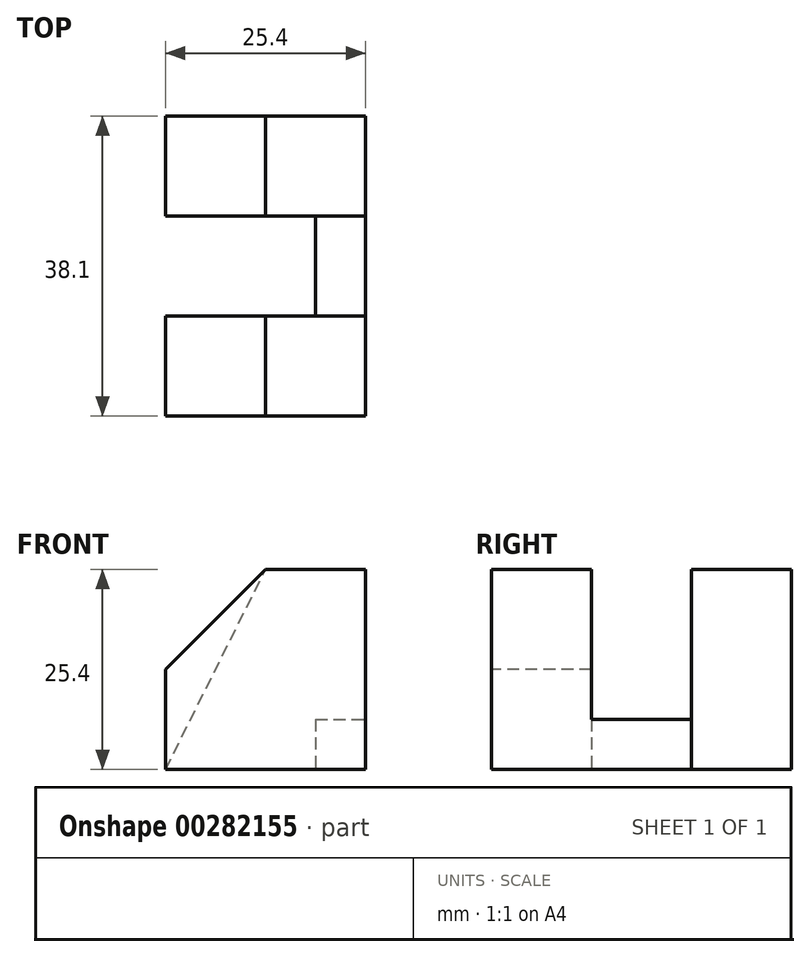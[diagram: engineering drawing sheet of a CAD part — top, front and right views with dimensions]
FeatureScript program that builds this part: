
annotation { "Feature Type Name" : "Feature", "Feature Type Description" : "" }
export const myFeature = defineFeature(function(context is Context, id is Id, definition is map)
    precondition{}
    {
        {
            var Q0;
            Q0=qCreatedBy(makeId("Front.planeOp"),FACE);
            var sketch = newSketch(context, id + "F0", { "sketchPlane" : qUnion([Q0])});
            skLineSegment(sketch, "E0", {"start": v(0, 0) * mm, "end": v(0, 25.4) * mm});
            skLineSegment(sketch, "E1", {"start": v(0, 25.4) * mm, "end": v(12.7, 25.4) * mm});
            skLineSegment(sketch, "E2", {"start": v(12.7, 25.4) * mm, "end": v(12.7, 0) * mm});
            skLineSegment(sketch, "E3", {"start": v(12.7, 0) * mm, "end": v(0, 0) * mm});
            skSolve(sketch);
        }
        {
            var Q0;
            Q0 = qSketchRegion(id + "F0", true);
            extrude(context, id + "F1", {"entities" : qUnion([Q0]), "depth" : 12.7 * mm});
        }
        {
            var Q0;
            Q0=makeQuery(id+"F1.opExtrude","CAP_FACE",FACE,{"disambiguationData":[OSD([sQuery(id+"F0.wireOp",EDGE,"E0"),sQuery(id+"F0.wireOp",EDGE,"E1"),sQuery(id+"F0.wireOp",EDGE,"E2"),sQuery(id+"F0.wireOp",EDGE,"E3")])],"isStart":false});
            var sketch = newSketch(context, id + "F2", { "sketchPlane" : qUnion([Q0])});
            skLineSegment(sketch, "E4", {"start": v(0, 0) * mm, "end": v(-12.7, 0) * mm});
            skLineSegment(sketch, "E5", {"start": v(-12.7, 0) * mm, "end": v(-12.7, 12.7) * mm});
            skLineSegment(sketch, "E6", {"start": v(-12.7, 12.7) * mm, "end": v(0, 12.7) * mm});
            skLineSegment(sketch, "E7", {"start": v(0, 12.7) * mm, "end": v(0, 0) * mm});
            skSolve(sketch);
        }
        {
            var Q0;
            Q0 = qSketchRegion(id + "F2", true);
            extrude(context, id + "F3", {"entities" : qUnion([Q0]), "operationType" : NewBodyOperationType.ADD, "oppositeDirection" : true, "depth" : 12.7 * mm});
        }
        {
            var Q0;
            Q0=makeQuery(id+"F3.boolean.opBoolean","MERGE",FACE,{"derivedFrom":[makeQuery(id+"F1.opExtrude","CAP_FACE",FACE,{"disambiguationData":[OSD([sQuery(id+"F0.wireOp",EDGE,"E0"),sQuery(id+"F0.wireOp",EDGE,"E1"),sQuery(id+"F0.wireOp",EDGE,"E2"),sQuery(id+"F0.wireOp",EDGE,"E3")])],"isStart":false}),makeQuery(id+"F3.opExtrude","CAP_FACE",FACE,{"disambiguationData":[OSD([sQuery(id+"F2.wireOp",EDGE,"E4"),sQuery(id+"F2.wireOp",EDGE,"E5"),sQuery(id+"F2.wireOp",EDGE,"E6"),sQuery(id+"F2.wireOp",EDGE,"E7")])],"isStart":true})]});
            var sketch = newSketch(context, id + "F4", { "sketchPlane" : qUnion([Q0])});
            skLineSegment(sketch, "E8", {"start": v(-12.7, 12.7) * mm, "end": v(0, 25.4) * mm});
            skSolve(sketch);
        }
        {
            var Q0;
            Q0=makeQuery(id+"F4.imprint","IMPRINT",FACE,{"disambiguationData":[TD([[makeQuery(id+"F4.imprint","IMPRINT",EDGE,{"derivedFrom":sQuery(id+"F4.wireOp",EDGE,"E8")}),-1.0]])]});
            extrude(context, id + "F5", {"entities" : qUnion([Q0]), "operationType" : NewBodyOperationType.ADD, "oppositeDirection" : true, "depth" : 12.7 * mm});
        }
        {
            var Q0;
            Q0=makeQuery(id+"F1.opExtrude","SWEPT_FACE",FACE,{"disambiguationData":[OSD([sQuery(id+"F0.wireOp",EDGE,"E2")])]});
            var sketch = newSketch(context, id + "F6", { "sketchPlane" : qUnion([Q0])});
            skLineSegment(sketch, "E9", {"start": v(0, 0) * mm, "end": v(12.7, 0) * mm});
            skLineSegment(sketch, "E10", {"start": v(0, 25.4) * mm, "end": v(0, 0) * mm});
            skLineSegment(sketch, "E11", {"start": v(12.7, 0) * mm, "end": v(12.7, 6.35) * mm});
            skLineSegment(sketch, "E12", {"start": v(12.7, 6.35) * mm, "end": v(0, 6.35) * mm});
            skSolve(sketch);
        }
        {
            var Q0;
            Q0 = qSketchRegion(id + "F6", true);
            extrude(context, id + "F7", {"entities" : qUnion([Q0]), "operationType" : NewBodyOperationType.ADD, "oppositeDirection" : true, "depth" : 6.35 * mm});
        }
        {
            var Q0;
            Q0=makeQuery(id+"F7.boolean.opBoolean","MERGE",FACE,{"derivedFrom":[makeQuery(id+"F3.boolean.opBoolean","MERGE",FACE,{"derivedFrom":[makeQuery(id+"F1.opExtrude","SWEPT_FACE",FACE,{"disambiguationData":[OSD([sQuery(id+"F0.wireOp",EDGE,"E3")])]}),makeQuery(id+"F3.opExtrude","SWEPT_FACE",FACE,{"disambiguationData":[OSD([sQuery(id+"F2.wireOp",EDGE,"E4")])]})]}),makeQuery(id+"F7.opExtrude","SWEPT_FACE",FACE,{"disambiguationData":[OSD([sQuery(id+"F6.wireOp",EDGE,"E9")])]})]});
            var sketch = newSketch(context, id + "F8", { "sketchPlane" : qUnion([Q0])});
            skLineSegment(sketch, "E13", {"start": v(12.7, -12.7) * mm, "end": v(12.7, -25.4) * mm});
            skLineSegment(sketch, "E14", {"start": v(12.7, -25.4) * mm, "end": v(0, -25.4) * mm});
            skLineSegment(sketch, "E15", {"start": v(0, -25.4) * mm, "end": v(0, -12.7) * mm});
            skLineSegment(sketch, "E16", {"start": v(0, -12.7) * mm, "end": v(12.7, -12.7) * mm});
            skSolve(sketch);
        }
        {
            var Q0;
            Q0 = qSketchRegion(id + "F8", true);
            extrude(context, id + "F9", {"entities" : qUnion([Q0]), "oppositeDirection" : true, "depth" : 25.4 * mm});
        }
        {
            var Q0;
            Q0=makeQuery(id+"F9.opExtrude","SWEPT_FACE",FACE,{"disambiguationData":[OSD([sQuery(id+"F8.wireOp",EDGE,"E14")])]});
            var sketch = newSketch(context, id + "F10", { "sketchPlane" : qUnion([Q0])});
            skLineSegment(sketch, "E17", {"start": v(0, 0) * mm, "end": v(12.7, 0) * mm});
            skLineSegment(sketch, "E18", {"start": v(12.7, 0) * mm, "end": v(0, 25.4) * mm});
            skSolve(sketch);
        }
        {
            var Q0;
            Q0=makeQuery(id+"F10.imprint","IMPRINT",FACE,{"disambiguationData":[TD([[makeQuery(id+"F10.imprint","IMPRINT",EDGE,{"derivedFrom":sQuery(id+"F10.wireOp",EDGE,"E17")}),1.0]])]});
            extrude(context, id + "F11", {"entities" : qUnion([Q0]), "operationType" : NewBodyOperationType.ADD, "oppositeDirection" : true, "depth" : 12.7 * mm});
        }
    });
